# Revit family: ProGlide UltraFlat™ Sliding Door_SG&DG- XXXX
name_source: partatom
category: Doors
units: mm (PartAtom-declared; Revit-internal decimal feet)

## family parameters
Always vertical = Yes
Cut with Voids When Loaded = No
Host = Wall
OmniClass Number = 23.30.20.00
OmniClass Title = Windows
Room Calculation Point = No
Shared = No

## types (5) — shared parameters
A = 45 mm  [stored 0.147638 ft]
Analytic Construction = <None>
Central Meeting = 11 mm  [stored 0.0360892 ft]
Define Thermal Properties by = Schematic Type
Ext Frame = 56.52 mm  [stored 0.185433 ft]
Head Offset = 10.5 mm
Head Offset 2 = 54.5 mm  [stored 0.178806 ft]
Manufacturer = ALSPEC
Model = ProGlide UltraFlat™ Sliding Door_SG&DG- XXXX
SG Fixed Panel Width = 901.25 mm
Stile A = 45 mm  [stored 0.147638 ft]
Wall Closure = By host
YEAR = 2022
zero-valued in all types: Default Sill Height, Height, Rough Height, Rough Width, Thickness, Width

## per-type parameters (varying)
| type | URL |
| OXXO_AD744+AD747/AD854+AD857 | https://www.alspec.com.au |
| OXXO_AD744+AD749/AD854+AD859 | WWW.ALSPEC.COM.AU |
| OXXO_AD747/AD857 | WWW.ALSPEC.COM.AU |
| OXXO_AD749/AD859 | WWW.ALSPEC.COM.AU |
| OXXO_AD744/AD854 | WWW.ALSPEC.COM.AU |

note: [stored X ft] marks values corroborated as IEEE doubles in the binary element streams (Revit-internal decimal feet)

## geometry (parser evidence)
native form markers: Sweep x62
no freeform markers — native parametric forms only
